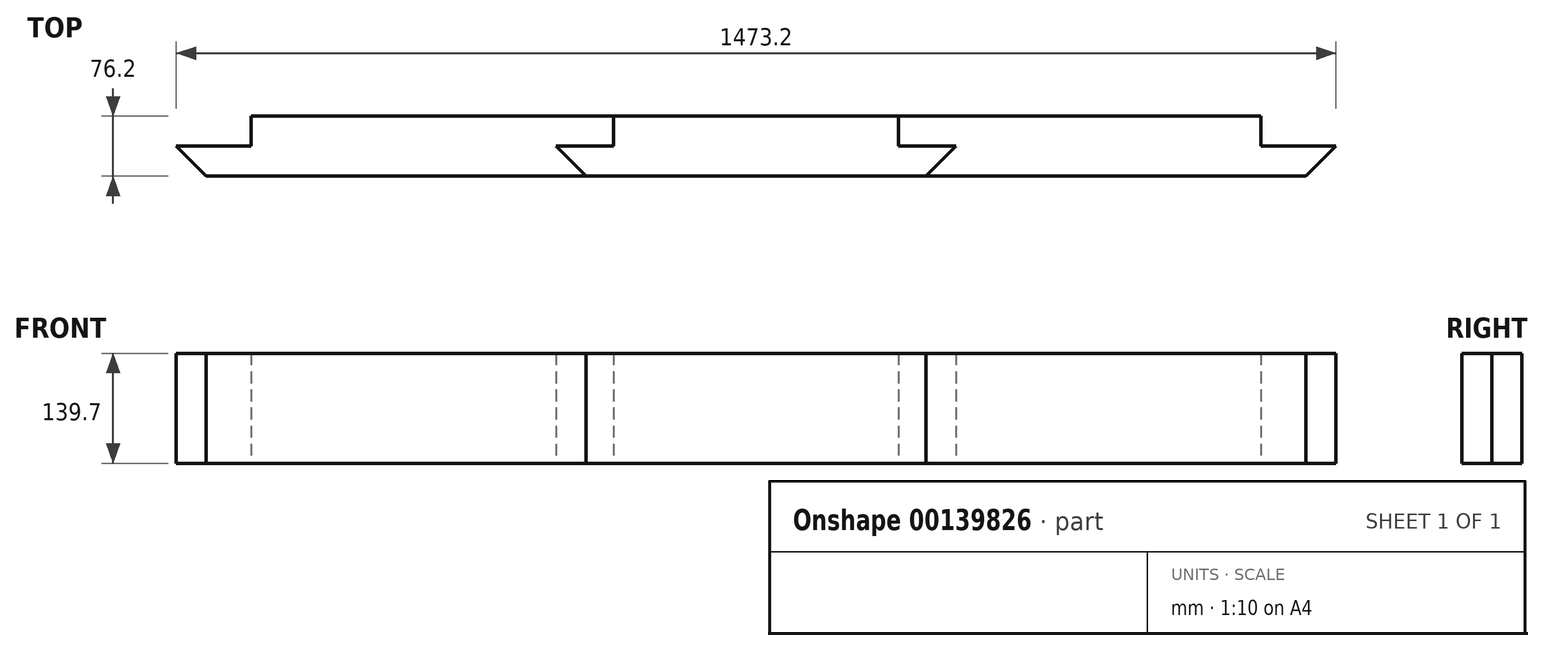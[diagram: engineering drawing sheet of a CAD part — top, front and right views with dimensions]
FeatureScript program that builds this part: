
annotation { "Feature Type Name" : "Feature", "Feature Type Description" : "" }
export const myFeature = defineFeature(function(context is Context, id is Id, definition is map)
    precondition{}
    {
        {
            var Q0;
            Q0=qCreatedBy(makeId("Top.planeOp"),FACE);
            var sketch = newSketch(context, id + "F0", { "sketchPlane" : qUnion([Q0])});
            skLineSegment(sketch, "E0", {"start": v(-698.5, -38.1) * mm, "end": v(698.5, -38.1) * mm});
            skLineSegment(sketch, "E1", {"start": v(698.5, -38.1) * mm, "end": v(736.6, 0) * mm});
            skLineSegment(sketch, "E2", {"start": v(736.6, 0) * mm, "end": v(641.35, 0) * mm});
            skLineSegment(sketch, "E3", {"start": v(641.35, 0) * mm, "end": v(641.35, 38.1) * mm});
            skLineSegment(sketch, "E4", {"start": v(641.35, 38.1) * mm, "end": v(-641.35, 38.1) * mm});
            skLineSegment(sketch, "E5", {"start": v(-641.35, 38.1) * mm, "end": v(-641.35, 0) * mm});
            skLineSegment(sketch, "E6", {"start": v(-641.35, 0) * mm, "end": v(-736.6, 0) * mm});
            skLineSegment(sketch, "E7", {"start": v(-736.6, 0) * mm, "end": v(-698.5, -38.1) * mm});
            skSolve(sketch);
        }
        {
            var Q0;
            Q0=makeQuery(id+"F0.imprint","IMPRINT",FACE,{"disambiguationData":[TD([[makeQuery(id+"F0.imprint","IMPRINT",EDGE,{"derivedFrom":sQuery(id+"F0.wireOp",EDGE,"E0")}),1.0]])]});
            extrude(context, id + "F1", {"entities" : qUnion([Q0]), "depth" : 139.7 * mm});
        }
        {
            var Q0;
            Q0=qCreatedBy(makeId("Top.planeOp"),FACE);
            var sketch = newSketch(context, id + "F2", { "sketchPlane" : qUnion([Q0])});
            skLineSegment(sketch, "E8", {"start": v(-215.9, -38.1) * mm, "end": v(215.9, -38.1) * mm});
            skLineSegment(sketch, "E9", {"start": v(215.9, -38.1) * mm, "end": v(254, 0) * mm});
            skLineSegment(sketch, "E10", {"start": v(254, 0) * mm, "end": v(180.98, 0) * mm});
            skLineSegment(sketch, "E11", {"start": v(180.98, 0) * mm, "end": v(180.98, 38.1) * mm});
            skLineSegment(sketch, "E12", {"start": v(180.98, 38.1) * mm, "end": v(-180.98, 38.1) * mm});
            skLineSegment(sketch, "E13", {"start": v(-180.98, 38.1) * mm, "end": v(-180.98, 0) * mm});
            skLineSegment(sketch, "E14", {"start": v(-180.97, 0) * mm, "end": v(-254, 0) * mm});
            skLineSegment(sketch, "E15", {"start": v(-254, 0) * mm, "end": v(-215.9, -38.1) * mm});
            skSolve(sketch);
        }
        {
            var Q0;
            Q0 = qSketchRegion(id + "F2", true);
            extrude(context, id + "F3", {"entities" : qUnion([Q0]), "depth" : 139.7 * mm});
        }
    });
